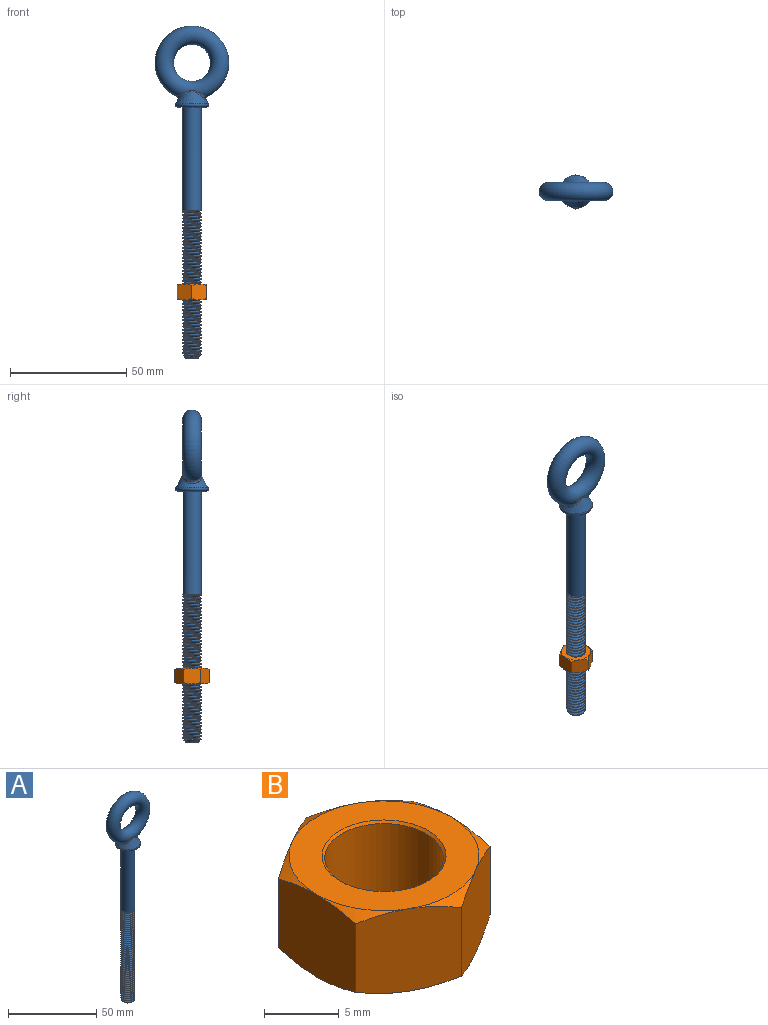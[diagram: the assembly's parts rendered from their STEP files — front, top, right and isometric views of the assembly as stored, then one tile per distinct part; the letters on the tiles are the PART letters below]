
ASSEMBLY  parts=2 mates=1
PART A: 59 faces, bbox 34.9x16x145.7 mm
  f0: torus R=11.91mm, axis (0,1,0), area 1744mm2, adj f1,f58
  f1: bspline ~12.3x6.51mm, area 19.9mm2, adj f0,f3,f58
  f2: torus R=6.15mm, axis (0,0,-1), area 88.3mm2, adj f3,f57
  f3: cone r=3.97mm half-angle=28.3deg, axis (0,0,-1), area 149.4mm2, adj f1,f2,f58
  f4: cone r=2.9mm half-angle=45deg, axis (0,0,1), area 17.9mm2, adj f49,f50,f51,f52,f53,f54,f55
  f5: cylinder r=3.97mm len=44.8mm, axis (0,0,1), area 1109.2mm2, adj f6,f51,f53,f56,f57
  f6: cylinder r=3.97mm len=7.94mm, axis (0,0,1), area 4.4mm2, adj f5,f7,f51,f53
  f7: cylinder r=3.97mm len=7.94mm, axis (0,0,1), area 4.4mm2, adj f6,f8,f51,f53
  f8: cylinder r=3.97mm len=7.94mm, axis (0,0,1), area 4.4mm2, adj f7,f9,f51,f53
  f9: cylinder r=3.97mm len=7.94mm, axis (0,0,1), area 4.4mm2, adj f8,f10,f51,f53
  f10: cylinder r=3.97mm len=7.94mm, axis (0,0,1), area 4.4mm2, adj f9,f11,f51,f53
  f11: cylinder r=3.97mm len=7.94mm, axis (0,0,1), area 4.4mm2, adj f10,f12,f51,f53
  f12: cylinder r=3.97mm len=7.94mm, axis (0,0,1), area 4.4mm2, adj f11,f13,f51,f53
  f13: cylinder r=3.97mm len=7.94mm, axis (0,0,1), area 4.4mm2, adj f12,f14,f51,f53
  f14: cylinder r=3.97mm len=7.94mm, axis (0,0,1), area 4.4mm2, adj f13,f15,f51,f53
  f15: cylinder r=3.97mm len=7.94mm, axis (0,0,1), area 4.4mm2, adj f14,f16,f51,f53
  f16: cylinder r=3.97mm len=7.94mm, axis (0,0,1), area 4.4mm2, adj f15,f17,f51,f53
  f17: cylinder r=3.97mm len=7.94mm, axis (0,0,1), area 4.4mm2, adj f16,f18,f51,f53
  f18: cylinder r=3.97mm len=7.94mm, axis (0,0,1), area 4.4mm2, adj f17,f19,f51,f53
  f19: cylinder r=3.97mm len=7.94mm, axis (0,0,1), area 4.4mm2, adj f18,f20,f51,f53
  f20: cylinder r=3.97mm len=7.94mm, axis (0,0,1), area 4.4mm2, adj f19,f21,f51,f53
  f21: cylinder r=3.97mm len=7.94mm, axis (0,0,1), area 4.4mm2, adj f20,f22,f51,f53
  f22: cylinder r=3.97mm len=7.94mm, axis (0,0,1), area 4.4mm2, adj f21,f23,f51,f53
  f23: cylinder r=3.97mm len=7.94mm, axis (0,0,1), area 4.4mm2, adj f22,f24,f51,f53
  f24: cylinder r=3.97mm len=7.94mm, axis (0,0,1), area 4.4mm2, adj f23,f25,f51,f53
  f25: cylinder r=3.97mm len=7.94mm, axis (0,0,1), area 4.4mm2, adj f24,f26,f51,f53
  f26: cylinder r=3.97mm len=7.94mm, axis (0,0,1), area 4.4mm2, adj f25,f27,f51,f53
  f27: cylinder r=3.97mm len=7.94mm, axis (0,0,1), area 4.4mm2, adj f26,f28,f51,f53
  f28: cylinder r=3.97mm len=7.94mm, axis (0,0,1), area 4.4mm2, adj f27,f29,f51,f53
  f29: cylinder r=3.97mm len=7.94mm, axis (0,0,1), area 4.4mm2, adj f28,f30,f51,f53
  f30: cylinder r=3.97mm len=7.94mm, axis (0,0,1), area 4.4mm2, adj f29,f31,f51,f53
  f31: cylinder r=3.97mm len=7.94mm, axis (0,0,1), area 4.4mm2, adj f30,f32,f51,f53
  f32: cylinder r=3.97mm len=7.94mm, axis (0,0,1), area 4.4mm2, adj f31,f33,f51,f53
  f33: cylinder r=3.97mm len=7.94mm, axis (0,0,1), area 4.4mm2, adj f32,f34,f51,f53
  f34: cylinder r=3.97mm len=7.94mm, axis (0,0,1), area 4.4mm2, adj f33,f35,f51,f53
  f35: cylinder r=3.97mm len=7.94mm, axis (0,0,1), area 4.4mm2, adj f34,f36,f51,f53
  f36: cylinder r=3.97mm len=7.94mm, axis (0,0,1), area 4.4mm2, adj f35,f37,f51,f53
  f37: cylinder r=3.97mm len=7.94mm, axis (0,0,1), area 4.4mm2, adj f36,f38,f51,f53
  f38: cylinder r=3.97mm len=7.94mm, axis (0,0,1), area 4.4mm2, adj f37,f39,f51,f53
  f39: cylinder r=3.97mm len=7.94mm, axis (0,0,1), area 4.4mm2, adj f38,f40,f51,f53
  f40: cylinder r=3.97mm len=7.94mm, axis (0,0,1), area 4.4mm2, adj f39,f41,f51,f53
  f41: cylinder r=3.97mm len=7.94mm, axis (0,0,1), area 4.4mm2, adj f40,f42,f51,f53
  f42: cylinder r=3.97mm len=7.94mm, axis (0,0,1), area 4.4mm2, adj f41,f43,f51,f53
  f43: cylinder r=3.97mm len=7.94mm, axis (0,0,1), area 4.4mm2, adj f42,f44,f51,f53
  f44: cylinder r=3.97mm len=7.94mm, axis (0,0,1), area 4.4mm2, adj f43,f45,f51,f53
  f45: cylinder r=3.97mm len=7.94mm, axis (0,0,1), area 4.4mm2, adj f44,f46,f51,f53
  f46: cylinder r=3.97mm len=7.94mm, axis (0,0,1), area 4.4mm2, adj f45,f47,f51,f53
  f47: cylinder r=3.97mm len=7.94mm, axis (0,0,1), area 4.4mm2, adj f46,f48,f51,f53
  f48: cylinder r=3.97mm len=7.94mm, axis (0,0,1), area 4.4mm2, adj f47,f49,f51,f53
  f49: cylinder r=3.97mm len=7.94mm, axis (0,0,1), area 4.4mm2, adj f4,f48,f50,f51,f52,f53
  f50: cylinder r=3.97mm len=2.66mm, axis (0,0,1), area 0.2mm2, adj f4,f49,f52
  f51: bspline ~64.96x8.09mm, area 1020.7mm2, adj f4,f5,f6,f7,f8,f9,f10,f11
  f52: bspline ~8.09x8.09mm, area 3.3mm2, adj f4,f49,f50
  f53: bspline ~64.07x8.09mm, area 1090.5mm2, adj f4,f5,f6,f7,f8,f9,f10,f11
  f54: cylinder r=3.05mm len=63.35mm, axis (0,0,-1), area 151.6mm2, adj f4,f51,f53,f56
  f55: plane 5.8x5.8mm, normal (0,0,-1), area 26.4mm2, adj f4
  f56: plane 8.48x8.48mm, normal (0,0,-1), area 10.4mm2, adj f5,f51,f53,f54
  f57: plane 12.3x12.3mm, normal (0,0,-1), area 69.4mm2, adj f2,f5
  f58: bspline ~12.32x6.53mm, area 20mm2, adj f0,f1,f3
PART B: 23 faces, bbox 14.7x14.7x6.7 mm
  f0: cylinder r=3.97mm len=7.94mm, axis (0,0,1), area 159.4mm2, adj f1,f2
  f1: cone r=4.15mm half-angle=45deg, axis (0,0,1), area 6.4mm2, adj f0,f4
  f2: cone r=3.97mm half-angle=45deg, axis (0,0,-1), area 6.4mm2, adj f0,f3
  f3: plane 12.7x12.7mm, normal (0,0,-1), area 72.7mm2, adj f2,f7,f8,f10,f12,f14,f16
  f4: plane 12.7x12.7mm, normal (0,0,1), area 72.7mm2, adj f1,f5,f6,f9,f11,f13,f15
  f5: cone r=7.33mm half-angle=60deg, axis (0,0,-1), area 2.5mm2, adj f4,f17,f22
  f6: cone r=7.33mm half-angle=60deg, axis (0,0,-1), area 2.5mm2, adj f4,f17,f18
  f7: cone r=6.35mm half-angle=60deg, axis (0,0,1), area 2.5mm2, adj f3,f17,f18
  f8: cone r=6.35mm half-angle=60deg, axis (0,0,1), area 2.5mm2, adj f3,f17,f22
  f9: cone r=7.33mm half-angle=60deg, axis (0,0,-1), area 2.5mm2, adj f4,f18,f19
  f10: cone r=6.35mm half-angle=60deg, axis (0,0,1), area 2.5mm2, adj f3,f18,f19
  f11: cone r=7.33mm half-angle=60deg, axis (0,0,-1), area 2.5mm2, adj f4,f19,f20
  f12: cone r=6.35mm half-angle=60deg, axis (0,0,1), area 2.5mm2, adj f3,f19,f20
  f13: cone r=7.33mm half-angle=60deg, axis (0,0,-1), area 2.5mm2, adj f4,f20,f21
  f14: cone r=6.35mm half-angle=60deg, axis (0,0,1), area 2.5mm2, adj f3,f20,f21
  f15: cone r=7.33mm half-angle=60deg, axis (0,0,-1), area 2.5mm2, adj f4,f21,f22
  f16: cone r=6.35mm half-angle=60deg, axis (0,0,1), area 2.5mm2, adj f3,f21,f22
  f17: plane 7.33x6.75mm, normal (1,0,0), area 46.6mm2, adj f5,f6,f7,f8,f18,f22
  f18: plane 6.75x6.35mm, normal (0.5,0.87,0), area 46.6mm2, adj f6,f7,f9,f10,f17,f19
  f19: plane 6.75x6.35mm, normal (-0.5,0.87,0), area 46.6mm2, adj f9,f10,f11,f12,f18,f20
  f20: plane 7.33x6.75mm, normal (-1,0,0), area 46.6mm2, adj f11,f12,f13,f14,f19,f21
  f21: plane 6.75x6.35mm, normal (-0.5,-0.87,0), area 46.6mm2, adj f13,f14,f15,f16,f20,f22
  f22: plane 6.75x6.35mm, normal (0.5,-0.87,0), area 46.6mm2, adj f5,f8,f15,f16,f17,f21
PLACE A t=(-37.56,-48.27,33.57)mm
PLACE B t=(-37.56,-48.27,45.87)mm
MATE fastened B.f7 <-> A.f54  axis (0,0,1) through (-37.56,-48.27,-61.68)mm
